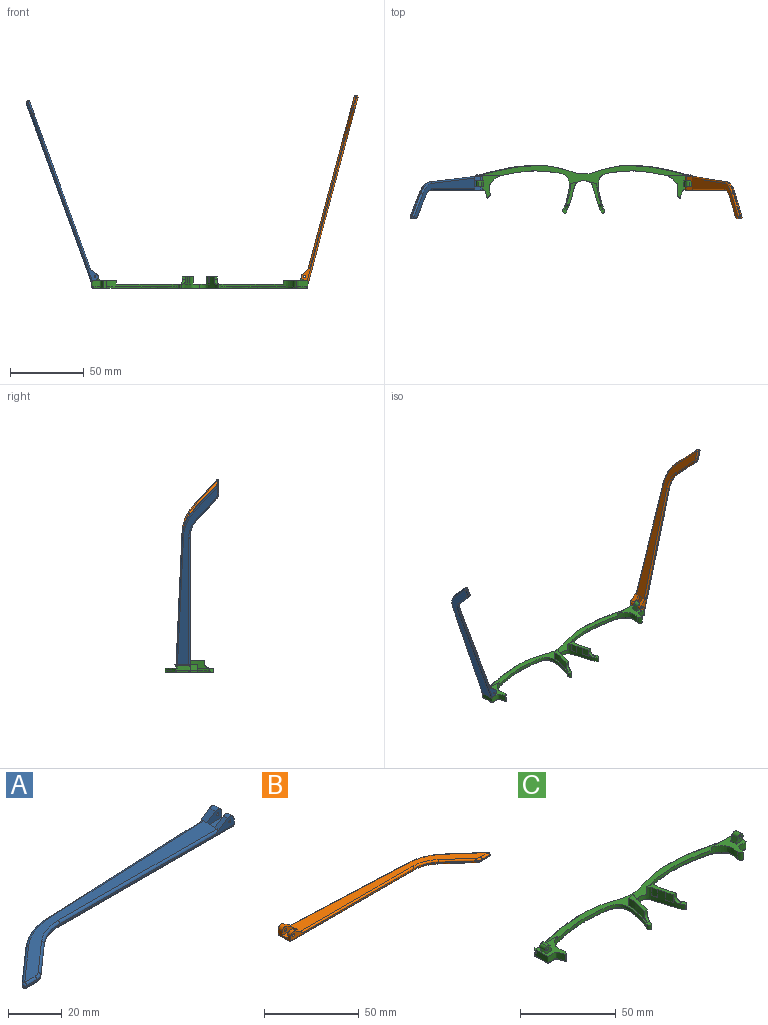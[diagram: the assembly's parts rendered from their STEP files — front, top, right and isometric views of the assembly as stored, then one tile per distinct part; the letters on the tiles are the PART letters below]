
ASSEMBLY  parts=3 mates=2
PART A: 43 faces, bbox 130.2x29.5x5.9 mm
  f0: plane 9.62x3.72mm, normal (1,0,0), area 24.7mm2, adj f1,f3,f4,f5,f10,f16,f18,f28
  f1: cylinder r=2.2mm len=3.45mm, axis (0,-1,0), area 11mm2, adj f0,f2,f4,f37
  f2: plane 6.01x3.91mm, normal (-0.55,0,0.84), area 12.7mm2, adj f1,f4,f9,f19,f37
  f3: plane 2.26x0.1mm, normal (0,0,1), area 0.1mm2, adj f0,f5,f18
  f4: plane 92.1x4.9mm, normal (0,-1,0), area 79.9mm2, adj f0,f1,f2,f14,f19,f36,f42
  f5: plane 93.42x4.13mm, normal (-0.04,1,0), area 64.8mm2, adj f0,f3,f11,f15,f17,f27,f28
  f6: plane 17.82x15.72mm, normal (-0.66,0.75,0), area 14.3mm2, adj f11,f12,f25,f30
  f7: plane 5.46x0.6mm, normal (0,-1,0), area 3.3mm2, adj f12,f13,f23,f32
  f8: plane 14.99x13.23mm, normal (0.66,-0.75,0), area 12mm2, adj f13,f14,f21,f34
  f9: plane 121.18x26.73mm, normal (0,0,1), area 627.7mm2, adj f2,f17,f19,f20,f21,f22,f23,f25
  f10: plane 129.1x27.08mm, normal (0,0,-1), area 686.5mm2, adj f0,f28,f29,f30,f32,f33,f34,f35
  f11: cylinder r=30mm len=18.52mm, axis (0,0,-1), area 12.2mm2, adj f5,f6,f26,f29
  f12: cylinder r=1mm len=1.75mm, axis (0,0,-1), area 1.5mm2, adj f6,f7,f24,f31
  f13: cylinder r=5mm len=3.31mm, axis (0,0,-1), area 2.2mm2, adj f7,f8,f22,f33
  f14: cylinder r=20mm len=13.23mm, axis (0,0,1), area 8.7mm2, adj f4,f8,f20,f35
  f15: plane 5.66x0.25mm, normal (0,0,-1), area 0.7mm2, adj f5,f17,f18
  f16: cylinder r=2.2mm len=3.45mm, axis (0,-1,0), area 14.8mm2, adj f0,f17,f18,f38
  f17: plane 6.01x3.91mm, normal (-0.55,0,0.84), area 16.9mm2, adj f5,f9,f15,f16,f18,f27,f38
  f18: plane 7.92x3.3mm, normal (0,1,0), area 15.9mm2, adj f0,f3,f15,f16,f17,f41
  f19: cylinder r=1mm len=84.18mm, axis (-1,0,0), area 131.4mm2, adj f2,f4,f9,f20
  f20: torus R=21mm, axis (0,0,1), area 23.1mm2, adj f9,f14,f19,f21
  f21: cylinder r=1mm len=15.65mm, axis (-0.75,-0.66,0), area 31.4mm2, adj f8,f9,f20,f22
  f22: torus R=4mm, axis (0,0,1), area 5.3mm2, adj f9,f13,f21,f23
  f23: cylinder r=1mm len=5.46mm, axis (-1,0,0), area 8.6mm2, adj f7,f9,f22,f24
  f24: sphere r=1mm, area 2.4mm2, adj f12,f23,f25
  f25: cylinder r=1mm len=18.48mm, axis (0.75,0.66,0), area 37.3mm2, adj f6,f9,f24,f26
  f26: torus R=29mm, axis (0,0,1), area 31.6mm2, adj f9,f11,f25,f27
  f27: cylinder r=1mm len=85.5mm, axis (1,0.04,0), area 133.5mm2, adj f5,f9,f17,f26
  f28: cylinder r=1mm len=93.46mm, axis (-1,-0.04,0), area 146.9mm2, adj f0,f5,f10,f29
  f29: torus R=29mm, axis (0,0,1), area 31.6mm2, adj f10,f11,f28,f30
  f30: cylinder r=1mm len=18.48mm, axis (-0.75,-0.66,0), area 37.3mm2, adj f6,f10,f29,f31
  f31: sphere r=1mm, area 2.4mm2, adj f12,f30,f32
  f32: cylinder r=1mm len=5.46mm, axis (1,0,0), area 8.6mm2, adj f7,f10,f31,f33
  f33: torus R=4mm, axis (0,0,1), area 5.3mm2, adj f10,f13,f32,f34
  f34: cylinder r=1mm len=15.65mm, axis (0.75,0.66,0), area 31.4mm2, adj f8,f10,f33,f35
  f35: torus R=21mm, axis (0,0,1), area 23.1mm2, adj f10,f14,f34,f36
  f36: cylinder r=1mm len=92.1mm, axis (1,0,0), area 144.7mm2, adj f0,f4,f10,f35
  f37: plane 7.92x4.7mm, normal (0,1,0), area 27mm2, adj f0,f1,f2,f39,f40,f42
  f38: plane 7.92x4.7mm, normal (0,-1,0), area 27mm2, adj f0,f16,f17,f39,f40,f41
  f39: plane 7.92x4.1mm, normal (0,0,1), area 32.5mm2, adj f0,f37,f38,f40
  f40: plane 4.1x1.4mm, normal (1,0,0), area 5.7mm2, adj f9,f37,f38,f39
  f41: cylinder r=0.5mm len=3.1mm, axis (0,-1,0), area 9.7mm2, adj f18,f38
  f42: cylinder r=0.5mm len=2.3mm, axis (0,-1,0), area 7.2mm2, adj f4,f37
PART B: 43 faces, bbox 130.2x29.5x5.9 mm
  f0: plane 9.62x3.72mm, normal (-1,0,0), area 24.7mm2, adj f1,f3,f4,f5,f10,f16,f18,f28
  f1: cylinder r=2.2mm len=3.45mm, axis (0,-1,0), area 11mm2, adj f0,f2,f4,f37
  f2: plane 6.01x3.91mm, normal (0.55,0,0.84), area 12.7mm2, adj f1,f4,f9,f19,f37
  f3: plane 2.26x0.1mm, normal (0,0,1), area 0.1mm2, adj f0,f5,f18
  f4: plane 92.1x4.9mm, normal (0,-1,0), area 78.2mm2, adj f0,f1,f2,f14,f19,f36,f42
  f5: plane 93.42x4.13mm, normal (0.04,1,0), area 64.8mm2, adj f0,f3,f11,f15,f17,f27,f28
  f6: plane 17.82x15.72mm, normal (0.66,0.75,0), area 14.3mm2, adj f11,f12,f25,f30
  f7: plane 5.46x0.6mm, normal (0,-1,0), area 3.3mm2, adj f12,f13,f23,f32
  f8: plane 14.99x13.23mm, normal (-0.66,-0.75,0), area 12mm2, adj f13,f14,f21,f34
  f9: plane 121.18x26.73mm, normal (0,0,1), area 627.7mm2, adj f2,f17,f19,f20,f21,f22,f23,f25
  f10: plane 129.1x27.08mm, normal (0,0,-1), area 686.5mm2, adj f0,f28,f29,f30,f32,f33,f34,f35
  f11: cylinder r=30mm len=18.52mm, axis (0,0,-1), area 12.2mm2, adj f5,f6,f26,f29
  f12: cylinder r=1mm len=1.75mm, axis (0,0,-1), area 1.5mm2, adj f6,f7,f24,f31
  f13: cylinder r=5mm len=3.31mm, axis (0,0,-1), area 2.2mm2, adj f7,f8,f22,f33
  f14: cylinder r=20mm len=13.23mm, axis (0,0,1), area 8.7mm2, adj f4,f8,f20,f35
  f15: plane 5.66x0.25mm, normal (0,0,-1), area 0.7mm2, adj f5,f17,f18
  f16: cylinder r=2.2mm len=3.45mm, axis (0,-1,0), area 14.8mm2, adj f0,f17,f18,f38
  f17: plane 6.01x3.91mm, normal (0.55,0,0.84), area 16.9mm2, adj f5,f9,f15,f16,f18,f27,f38
  f18: plane 7.92x3.3mm, normal (0,1,0), area 14.3mm2, adj f0,f3,f15,f16,f17,f41
  f19: cylinder r=1mm len=84.18mm, axis (1,0,0), area 131.4mm2, adj f2,f4,f9,f20
  f20: torus R=21mm, axis (0,0,1), area 23.1mm2, adj f9,f14,f19,f21
  f21: cylinder r=1mm len=15.65mm, axis (0.75,-0.66,0), area 31.4mm2, adj f8,f9,f20,f22
  f22: torus R=4mm, axis (0,0,1), area 5.3mm2, adj f9,f13,f21,f23
  f23: cylinder r=1mm len=5.46mm, axis (1,0,0), area 8.6mm2, adj f7,f9,f22,f24
  f24: sphere r=1mm, area 2.4mm2, adj f12,f23,f25
  f25: cylinder r=1mm len=18.48mm, axis (-0.75,0.66,0), area 37.3mm2, adj f6,f9,f24,f26
  f26: torus R=29mm, axis (0,0,1), area 31.6mm2, adj f9,f11,f25,f27
  f27: cylinder r=1mm len=85.5mm, axis (-1,0.04,0), area 133.5mm2, adj f5,f9,f17,f26
  f28: cylinder r=1mm len=93.46mm, axis (1,-0.04,0), area 146.9mm2, adj f0,f5,f10,f29
  f29: torus R=29mm, axis (0,0,1), area 31.6mm2, adj f10,f11,f28,f30
  f30: cylinder r=1mm len=18.48mm, axis (0.75,-0.66,0), area 37.3mm2, adj f6,f10,f29,f31
  f31: sphere r=1mm, area 2.4mm2, adj f12,f30,f32
  f32: cylinder r=1mm len=5.46mm, axis (-1,0,0), area 8.6mm2, adj f7,f10,f31,f33
  f33: torus R=4mm, axis (0,0,1), area 5.3mm2, adj f10,f13,f32,f34
  f34: cylinder r=1mm len=15.65mm, axis (-0.75,0.66,0), area 31.4mm2, adj f8,f10,f33,f35
  f35: torus R=21mm, axis (0,0,1), area 23.1mm2, adj f10,f14,f34,f36
  f36: cylinder r=1mm len=92.1mm, axis (-1,0,0), area 144.7mm2, adj f0,f4,f10,f35
  f37: plane 7.92x4.7mm, normal (0,1,0), area 25.4mm2, adj f0,f1,f2,f39,f40,f42
  f38: plane 7.92x4.7mm, normal (0,-1,0), area 25.4mm2, adj f0,f16,f17,f39,f40,f41
  f39: plane 7.92x4.1mm, normal (0,0,1), area 32.5mm2, adj f0,f37,f38,f40
  f40: plane 4.1x1.4mm, normal (-1,0,0), area 5.7mm2, adj f9,f37,f38,f39
  f41: cylinder r=0.88mm len=3.1mm, axis (0,-1,0), area 17mm2, adj f18,f38
  f42: cylinder r=0.88mm len=2.3mm, axis (0,-1,0), area 12.6mm2, adj f4,f37
PART C: 90 faces, bbox 148.3x33.4x10 mm
  f0: plane 0.12x0.12mm, normal (0,0,1), area 0mm2, adj f32,f42
  f1: plane 2.1x0.76mm, normal (-1,0,0), area 0.8mm2, adj f20,f21,f32
  f2: plane 2.1x0.76mm, normal (-0.09,-1,0), area 0.8mm2, adj f8,f21,f32
  f3: plane 3.72x1.06mm, normal (0,0,1), area 0.1mm2, adj f10,f38
  f4: plane 144.56x32.9mm, normal (0,0,1), area 579.9mm2, adj f6,f9,f10,f11,f20,f35,f36,f37
  f5: plane 4.46x1.45mm, normal (0,0,1), area 0.1mm2, adj f10,f33
  f6: extruded ~54.16x26.41mm, area 205.9mm2, adj f4,f7,f11,f19,f20,f21
  f7: cylinder r=4mm len=5.1mm, axis (0,0,-1), area 15.9mm2, adj f6,f8,f12,f13,f19,f21
  f8: extruded ~38.03x22.18mm, area 153.1mm2, adj f2,f7,f9,f13,f14,f15,f16,f17
  f9: extruded ~35.39x5.69mm, area 71.4mm2, adj f4,f8,f18,f45,f54
  f10: extruded ~22.32x12.62mm, area 122.9mm2, adj f3,f4,f5,f11,f12,f33,f34,f37
  f11: cylinder r=2.23mm len=3mm, axis (0,0,-1), area 9.4mm2, adj f4,f6,f10,f12,f19
  f12: plane 144.79x31.79mm, normal (0,0,-1), area 557mm2, adj f7,f10,f11,f13,f15,f17,f18,f19
  f13: bspline ~8.38x7.57mm, area 17.2mm2, adj f7,f8,f12,f14
  f14: bspline ~1x1mm, area 0.8mm2, adj f8,f13,f15
  f15: bspline ~8.55x1.2mm, area 12.6mm2, adj f8,f12,f14,f16
  f16: bspline ~1.04x1mm, area 0.7mm2, adj f8,f15,f17
  f17: bspline ~41.91x8.32mm, area 59.8mm2, adj f8,f12,f16,f18
  f18: bspline ~38.48x6.7mm, area 56.6mm2, adj f9,f12,f17,f62
  f19: bspline ~56.23x29.54mm, area 139.1mm2, adj f6,f7,f11,f12
  f20: plane 15.61x2.1mm, normal (0,1,0), area 32.8mm2, adj f1,f4,f6,f21,f44
  f21: plane 17.48x15.78mm, normal (0,0,1), area 103.9mm2, adj f1,f2,f6,f7,f8,f20,f22,f23
  f22: plane 0.73x0.26mm, normal (0,-1,0), area 0.1mm2, adj f21,f23,f25,f26
  f23: plane 4x0.26mm, normal (-1,0,0), area 1.1mm2, adj f21,f22,f24,f25
  f24: plane 5.07x4.86mm, normal (0,1,0), area 15.8mm2, adj f21,f23,f25,f27,f28,f29,f30,f31
  f25: plane 4x0.05mm, normal (0.34,0,0.94), area 0.2mm2, adj f22,f23,f24,f27
  f26: plane 5.02x4.86mm, normal (0,-1,0), area 15.7mm2, adj f21,f22,f27,f28,f29,f30,f31
  f27: plane 4x3.31mm, normal (-0.94,0,0.34), area 14.1mm2, adj f24,f25,f26,f30
  f28: plane 4x2.21mm, normal (0.94,0,-0.34), area 9.4mm2, adj f21,f24,f26,f29
  f29: cylinder r=1.98mm len=4mm, axis (0,-1,0), area 12.4mm2, adj f24,f26,f28,f30
  f30: cylinder r=1.98mm len=4mm, axis (0,1,0), area 12.4mm2, adj f24,f26,f27,f29
  f31: cylinder r=0.88mm len=4mm, axis (0,-1,0), area 22mm2, adj f24,f26
  f32: cone r=1mm half-angle=20deg, axis (0,0,1), area 5.1mm2, adj f0,f1,f2,f21,f41,f43
  f33: extruded ~5x4.44mm, area 23.3mm2, adj f5,f10,f39
  f34: plane 2.1x2mm, normal (0,-1,0), area 4.2mm2, adj f10,f35,f39,f40
  f35: extruded ~17.45x5mm, area 78.9mm2, adj f4,f34,f36,f39,f40
  f36: plane 5x4.38mm, normal (0.14,0.99,0), area 22.1mm2, adj f4,f35,f37,f39
  f37: extruded ~5x0.06mm, area 0.4mm2, adj f4,f10,f36,f39
  f38: extruded ~5x3.64mm, area 18.9mm2, adj f3,f10,f39
  f39: plane 15.19x7.44mm, normal (0,0,1), area 35.5mm2, adj f10,f33,f34,f35,f36,f37,f38
  f40: cylinder r=3mm len=3.05mm, axis (1,0,0), area 9.5mm2, adj f4,f10,f34,f35
  f41: bspline ~0.75x0.3mm, area 0.1mm2, adj f8,f32,f42
  f42: bspline ~0.44x0.42mm, area 0.2mm2, adj f0,f8,f41,f43
  f43: bspline ~1.05x0.58mm, area 0.3mm2, adj f8,f32,f42,f44
  f44: bspline ~0.42x0.33mm, area 0mm2, adj f8,f20,f43,f45
  f45: bspline ~45.86x7.84mm, area 18.8mm2, adj f4,f8,f9,f44
  f46: plane 0.12x0.12mm, normal (0,0,1), area 0mm2, adj f76,f86
  f47: plane 2.1x0.76mm, normal (1,0,0), area 0.8mm2, adj f64,f65,f76
  f48: plane 2.1x0.76mm, normal (0.09,-1,0), area 0.8mm2, adj f53,f65,f76
  f49: plane 3.72x1.06mm, normal (0,0,1), area 0.1mm2, adj f55,f82
  f50: plane 4.46x1.45mm, normal (0,0,1), area 0.1mm2, adj f55,f77
  f51: extruded ~54.16x26.41mm, area 205.9mm2, adj f4,f52,f56,f63,f64,f65
  f52: cylinder r=4mm len=5.1mm, axis (0,0,-1), area 15.9mm2, adj f12,f51,f53,f57,f63,f65
  f53: extruded ~38.03x22.18mm, area 153.1mm2, adj f48,f52,f54,f57,f58,f59,f60,f61
  f54: extruded ~35.39x5.69mm, area 71.4mm2, adj f4,f9,f53,f62,f89
  f55: extruded ~22.32x12.62mm, area 122.9mm2, adj f4,f10,f12,f49,f50,f56,f77,f78
  f56: cylinder r=2.23mm len=3mm, axis (0,0,-1), area 9.4mm2, adj f4,f12,f51,f55,f63
  f57: bspline ~8.38x7.57mm, area 17.2mm2, adj f12,f52,f53,f58
  f58: bspline ~1x1mm, area 0.8mm2, adj f53,f57,f59
  f59: bspline ~8.55x1.2mm, area 12.6mm2, adj f12,f53,f58,f60
  f60: bspline ~1.04x1mm, area 0.8mm2, adj f53,f59,f61
  f61: bspline ~41.91x8.32mm, area 59.8mm2, adj f12,f53,f60,f62
  f62: bspline ~38.48x6.7mm, area 56.6mm2, adj f12,f18,f54,f61
  f63: bspline ~56.23x29.54mm, area 139.1mm2, adj f12,f51,f52,f56
  f64: plane 15.61x2.1mm, normal (0,1,0), area 32.8mm2, adj f4,f47,f51,f65,f88
  f65: plane 17.48x15.78mm, normal (0,0,1), area 103.9mm2, adj f47,f48,f51,f52,f53,f64,f66,f67
  f66: plane 0.73x0.26mm, normal (0,-1,0), area 0.1mm2, adj f65,f67,f69,f70
  f67: plane 4x0.26mm, normal (1,0,0), area 1.1mm2, adj f65,f66,f68,f69
  f68: plane 5.07x4.86mm, normal (0,1,0), area 15.8mm2, adj f65,f67,f69,f71,f72,f73,f74,f75
  f69: plane 4x0.05mm, normal (-0.34,0,0.94), area 0.2mm2, adj f66,f67,f68,f71
  f70: plane 5.02x4.86mm, normal (0,-1,0), area 15.7mm2, adj f65,f66,f71,f72,f73,f74,f75
  f71: plane 4x3.31mm, normal (0.94,0,0.34), area 14.1mm2, adj f68,f69,f70,f74
  f72: plane 4x2.21mm, normal (-0.94,0,-0.34), area 9.4mm2, adj f65,f68,f70,f73
  f73: cylinder r=1.98mm len=4mm, axis (0,-1,0), area 12.4mm2, adj f68,f70,f72,f74
  f74: cylinder r=1.98mm len=4mm, axis (0,1,0), area 12.4mm2, adj f68,f70,f71,f73
  f75: cylinder r=0.88mm len=4mm, axis (0,-1,0), area 22mm2, adj f68,f70
  f76: cone r=1mm half-angle=20deg, axis (0,0,1), area 5.1mm2, adj f46,f47,f48,f65,f85,f87
  f77: extruded ~5x4.44mm, area 23.3mm2, adj f50,f55,f83
  f78: plane 2.1x2mm, normal (0,-1,0), area 4.2mm2, adj f55,f79,f83,f84
  f79: extruded ~17.45x5mm, area 78.9mm2, adj f4,f78,f80,f83,f84
  f80: plane 5x4.38mm, normal (-0.14,0.99,0), area 22.1mm2, adj f4,f79,f81,f83
  f81: extruded ~5x0.06mm, area 0.4mm2, adj f4,f55,f80,f83
  f82: extruded ~5x3.64mm, area 18.9mm2, adj f49,f55,f83
  f83: plane 15.19x7.44mm, normal (0,0,1), area 35.5mm2, adj f55,f77,f78,f79,f80,f81,f82
  f84: cylinder r=3mm len=3.05mm, axis (-1,0,0), area 9.5mm2, adj f4,f55,f78,f79
  f85: bspline ~0.75x0.3mm, area 0.1mm2, adj f53,f76,f86
  f86: bspline ~0.44x0.42mm, area 0.2mm2, adj f46,f53,f85,f87
  f87: bspline ~1.05x0.58mm, area 0.3mm2, adj f53,f76,f86,f88
  f88: bspline ~0.42x0.33mm, area 0mm2, adj f53,f64,f87,f89
  f89: bspline ~45.86x7.84mm, area 18.8mm2, adj f4,f53,f54,f88
PLACE A rot(axis=(0,1,0),70deg) t=(-84.8,-5.75,55.99)mm
PLACE B rot(axis=(0,-1,0),75deg) t=(68.2,-5.75,-61.61)mm
PLACE C t=(10.15,-1.13,-5.77)mm
MATE revolute A.f1 <-> C.f74  axis (0,-1,0) through (-60.92,2.72,1.21)mm
MATE revolute B.f41 <-> C.f29  axis (0,-1,0) through (81.2,2.72,1.21)mm
